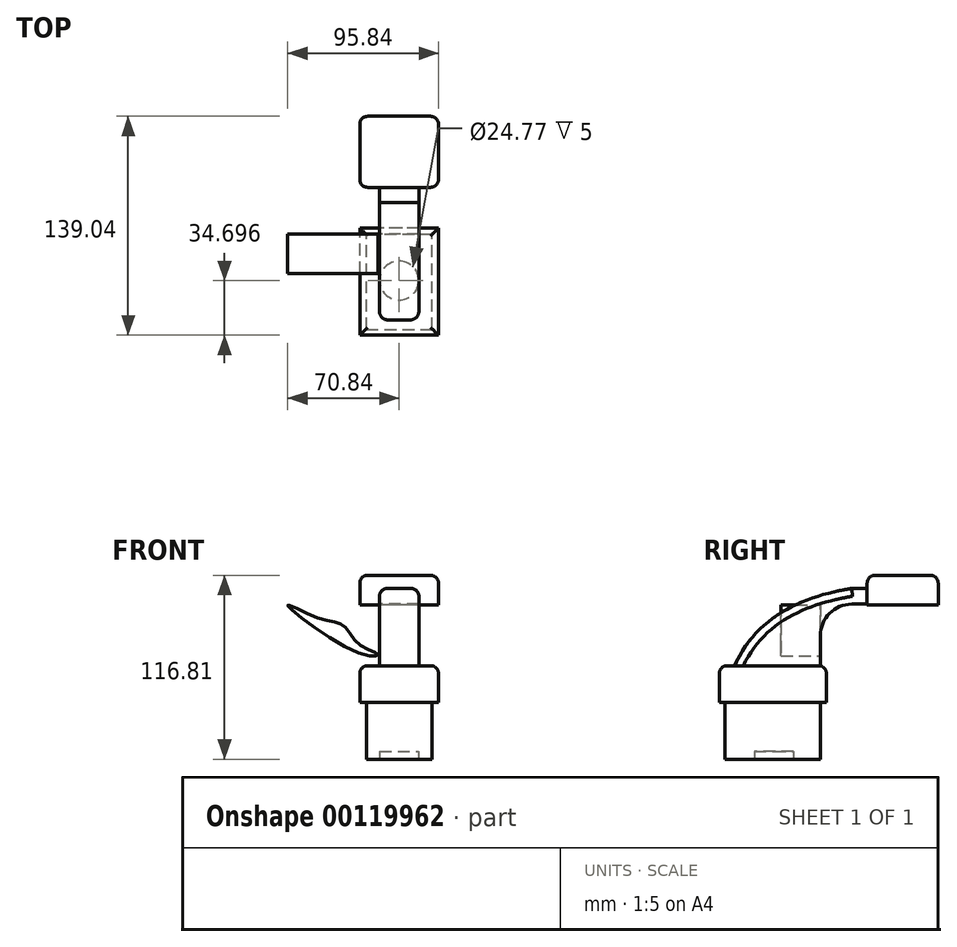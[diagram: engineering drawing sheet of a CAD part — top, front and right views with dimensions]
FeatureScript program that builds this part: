
annotation { "Feature Type Name" : "Feature", "Feature Type Description" : "" }
export const myFeature = defineFeature(function(context is Context, id is Id, definition is map)
    precondition{}
    {
        {
            var Q0;
            Q0=qCreatedBy(makeId("Right.planeOp"),FACE);
            var sketch = newSketch(context, id + "F0", { "sketchPlane" : qUnion([Q0])});
            skLineSegment(sketch, "E0.bottom", {"start": v(-64.19, 7.38) * mm, "end": v(3.9, 7.38) * mm});
            skLineSegment(sketch, "E0.top", {"start": v(-64.19, -16) * mm, "end": v(3.9, -16) * mm});
            skLineSegment(sketch, "E0.left", {"start": v(-64.19, 7.38) * mm, "end": v(-64.19, -16) * mm});
            skLineSegment(sketch, "E0.right", {"start": v(3.9, 7.38) * mm, "end": v(3.9, -16) * mm});
            skLineSegment(sketch, "E1.bottom", {"start": v(29.74, 64.8) * mm, "end": v(74.85, 64.8) * mm});
            skLineSegment(sketch, "E1.top", {"start": v(29.74, 45.94) * mm, "end": v(74.85, 45.94) * mm});
            skLineSegment(sketch, "E1.left", {"start": v(29.74, 64.8) * mm, "end": v(29.74, 45.94) * mm});
            skLineSegment(sketch, "E1.right", {"start": v(74.85, 64.8) * mm, "end": v(74.85, 45.94) * mm});
            skLineSegment(sketch, "E2", {"start": v(0, 0) * mm, "end": v(0, 7.38) * mm});
            skLineSegment(sketch, "E3", {"start": v(0, 0) * mm, "end": v(0, 26.48) * mm});
            skLineSegment(sketch, "E4", {"start": v(20, 46.48) * mm, "end": v(29.74, 46.48) * mm});
            skPoint(sketch, "E5.visualSharp", {"position": v(0, 46.48) * mm});
            skArc(sketch, "E5.filletArc", {"start": v(20, 46.48) * mm, "mid": v(5.86, 40.62) * mm, "end": v(0, 26.48) * mm});
            skLineSegment(sketch, "E6.0", {"start": v(-10, 7.38) * mm, "end": v(-10, 31.5) * mm});
            skLineSegment(sketch, "E7.0", {"start": v(20, 56.48) * mm, "end": v(29.74, 56.48) * mm});
            skArc(sketch, "E7.1", {"start": v(20, 56.48) * mm, "mid": v(0.62, 49.38) * mm, "end": v(-9.59, 31.44) * mm});
            skFitSpline(sketch, "E8", {"points": [v(-55.2, 5.58) * mm, v(20, 56.48) * mm], "startDerivative": vector(36.64, 85.75) * mm, "endDerivative": vector(116.03, 18.83) * mm});
            skSolve(sketch);
        }
        {
            var Q0;
            Q0=makeQuery(id+"F0.imprint","IMPRINT",FACE,{"disambiguationData":[TD([[makeQuery(id+"F0.imprint","IMPRINT",EDGE,{"derivedFrom":sQuery(id+"F0.wireOp",EDGE,"E0.top")}),1.0]])]});
            extrude(context, id + "F1", {"entities" : qUnion([Q0]), "endBound" : BoundingType.SYMMETRIC, "depth" : 50 * mm});
        }
        {
            var Q0;
            {var subQ4=sQuery(id+"F0.wireOp",EDGE,"E4");Q0=makeQuery(id+"F0.imprint","IMPRINT",FACE,{"disambiguationData":[TD([[makeQuery(id+"F0.imprint","IMPRINT",EDGE,{"derivedFrom":subQ4}),1.0]])]});}
            extrude(context, id + "F2", {"entities" : qUnion([Q0]), "operationType" : NewBodyOperationType.ADD, "endBound" : BoundingType.SYMMETRIC, "depth" : 25 * mm});
        }
        {
            var Q0;
            {var subQ3=sQuery(id+"F0.wireOp",EDGE,"E1.bottom");Q0=makeQuery(id+"F0.imprint","IMPRINT",FACE,{"disambiguationData":[TD([[makeQuery(id+"F0.imprint","IMPRINT",EDGE,{"derivedFrom":subQ3}),-1.0]])]});}
            extrude(context, id + "F3", {"entities" : qUnion([Q0]), "operationType" : NewBodyOperationType.ADD, "endBound" : BoundingType.SYMMETRIC, "depth" : 50 * mm});
        }
        {
            var Q0;
            Q0=makeQuery(id+"F1.opExtrude","CAP_EDGE",EDGE,{"disambiguationData":[OSD([sQuery(id+"F0.wireOp",EDGE,"E0.bottom")])],"isStart":true});
            var Q1;
            Q1=makeQuery(id+"F1.opExtrude","SWEPT_EDGE",EDGE,{"disambiguationData":[OSD([sQuery(id+"F0.wireOp",EDGE,"E0.bottom"),sQuery(id+"F0.wireOp",EDGE,"E0.right")])]});
            var Q2;
            Q2=makeQuery(id+"F1.opExtrude","SWEPT_EDGE",EDGE,{"disambiguationData":[OSD([sQuery(id+"F0.wireOp",EDGE,"E0.bottom"),sQuery(id+"F0.wireOp",EDGE,"E0.left")])]});
            var Q3;
            Q3=makeQuery(id+"F1.opExtrude","CAP_EDGE",EDGE,{"disambiguationData":[OSD([sQuery(id+"F0.wireOp",EDGE,"E0.bottom")])],"isStart":false});
            fillet(context, id + "F4", {"entities" : qUnion([Q0, Q1, Q2, Q3]), "radius" : 5 * mm, "tangentPropagation" : true, "allowEdgeOverflow" : false});
        }
        {
            var Q0;
            Q0=makeQuery(id+"F3.opExtrude","CAP_EDGE",EDGE,{"disambiguationData":[OSD([sQuery(id+"F0.wireOp",EDGE,"E1.bottom")])],"isStart":false});
            var Q1;
            Q1=makeQuery(id+"F3.opExtrude","CAP_EDGE",EDGE,{"disambiguationData":[OSD([sQuery(id+"F0.wireOp",EDGE,"E1.bottom")])],"isStart":true});
            var Q2;
            Q2=makeQuery(id+"F3.opExtrude","SWEPT_EDGE",EDGE,{"disambiguationData":[OSD([sQuery(id+"F0.wireOp",EDGE,"E1.bottom"),sQuery(id+"F0.wireOp",EDGE,"E1.right")])]});
            var Q3;
            Q3=makeQuery(id+"F3.opExtrude","CAP_EDGE",EDGE,{"disambiguationData":[OSD([sQuery(id+"F0.wireOp",EDGE,"E1.left")])],"isStart":true});
            var Q4;
            Q4=makeQuery(id+"F3.opExtrude","CAP_EDGE",EDGE,{"disambiguationData":[OSD([sQuery(id+"F0.wireOp",EDGE,"E1.left")])],"isStart":false});
            var Q5;
            Q5=makeQuery(id+"F3.opExtrude","CAP_EDGE",EDGE,{"disambiguationData":[OSD([sQuery(id+"F0.wireOp",EDGE,"E1.right")])],"isStart":false});
            var Q6;
            Q6=makeQuery(id+"F3.opExtrude","CAP_EDGE",EDGE,{"disambiguationData":[OSD([sQuery(id+"F0.wireOp",EDGE,"E1.right")])],"isStart":true});
            var Q7;
            Q7=makeQuery(id+"F3.opExtrude","SWEPT_EDGE",EDGE,{"disambiguationData":[OSD([sQuery(id+"F0.wireOp",EDGE,"E1.bottom"),sQuery(id+"F0.wireOp",EDGE,"E1.left")])]});
            fillet(context, id + "F5", {"entities" : qUnion([Q0, Q1, Q2, Q3, Q4, Q5, Q6, Q7]), "radius" : 5 * mm, "tangentPropagation" : true, "allowEdgeOverflow" : false});
        }
        {
            var Q0;
            Q0=makeQuery(id+"F2.opExtrude","CAP_EDGE",EDGE,{"disambiguationData":[OSD([sQuery(id+"F0.wireOp",EDGE,"E8")])],"isStart":false});
            var Q1;
            Q1=makeQuery(id+"F2.opExtrude","CAP_EDGE",EDGE,{"disambiguationData":[OSD([sQuery(id+"F0.wireOp",EDGE,"E7.0")])],"isStart":false});
            var Q2;
            Q2=makeQuery(id+"F2.opExtrude","CAP_EDGE",EDGE,{"disambiguationData":[OSD([sQuery(id+"F0.wireOp",EDGE,"E8")])],"isStart":true});
            var Q3;
            Q3=makeQuery(id+"F2.opExtrude","CAP_EDGE",EDGE,{"disambiguationData":[OSD([sQuery(id+"F0.wireOp",EDGE,"E7.0")])],"isStart":true});
            fillet(context, id + "F6", {"entities" : qUnion([Q0, Q1, Q2, Q3]), "radius" : 5 * mm, "tangentPropagation" : true, "allowEdgeOverflow" : false});
        }
        {
            var Q0;
            Q0=qCreatedBy(makeId("Top.planeOp"),FACE);
            var sketch = newSketch(context, id + "F7", { "sketchPlane" : qUnion([Q0])});
            skLineSegment(sketch, "E9.bottom", {"start": v(-20.83, -60.55) * mm, "end": v(20.92, -60.55) * mm});
            skLineSegment(sketch, "E9.top", {"start": v(-20.83, 0) * mm, "end": v(20.92, 0) * mm});
            skLineSegment(sketch, "E9.left", {"start": v(-20.83, -60.55) * mm, "end": v(-20.83, 0) * mm});
            skLineSegment(sketch, "E9.right", {"start": v(20.92, -60.55) * mm, "end": v(20.92, 0) * mm});
            skSolve(sketch);
        }
        {
            var Q0;
            Q0 = qSketchRegion(id + "F7", true);
            extrude(context, id + "F8", {"entities" : qUnion([Q0]), "operationType" : NewBodyOperationType.ADD, "oppositeDirection" : true, "depth" : 52 * mm});
        }
        {
            var Q0;
            Q0=makeQuery(id+"F8.opExtrude","CAP_FACE",FACE,{"disambiguationData":[OSD([sQuery(id+"F7.wireOp",EDGE,"E9.bottom"),sQuery(id+"F7.wireOp",EDGE,"E9.top"),sQuery(id+"F7.wireOp",EDGE,"E9.left"),sQuery(id+"F7.wireOp",EDGE,"E9.right")])],"isStart":false});
            var sketch = newSketch(context, id + "F9", { "sketchPlane" : qUnion([Q0])});
            skCircle(sketch, "E10", {"center": v(0, 29.5) * mm, "radius": 12.39 * mm});
            skSolve(sketch);
        }
        {
            var Q0;
            Q0 = qSketchRegion(id + "F9", true);
            extrude(context, id + "F10", {"entities" : qUnion([Q0]), "operationType" : NewBodyOperationType.REMOVE, "oppositeDirection" : true, "depth" : 5 * mm});
        }
        {
            var Q0;
            Q0=qCreatedBy(makeId("Front.planeOp"),FACE);
            var sketch = newSketch(context, id + "F11", { "sketchPlane" : qUnion([Q0])});
            skFitSpline(sketch, "E11", {"points": [v(-24.44, 20.27) * mm, v(-35.61, 32.87) * mm, v(-50.98, 37.5) * mm, v(-70.84, 45.9) * mm, v(-24.92, 15.09) * mm, v(-13.33, 14.65) * mm, v(-24.44, 20.27) * mm]});
            skSolve(sketch);
        }
        {
            var Q0;
            Q0=makeQuery(id+"F11.imprint","IMPRINT",FACE,{"disambiguationData":[TD([[makeQuery(id+"F11.imprint","IMPRINT",EDGE,{"derivedFrom":sQuery(id+"F11.wireOp",EDGE,"E11")}),1.0]])]});
            var Q1;
            Q1=sQuery(id+"F11.wireOp",EDGE,"E11");
            extrude(context, id + "F12", {"entities" : qUnion([Q0]), "surfaceEntities" : qUnion([Q1]), "depth" : 25 * mm});
        }
    });
